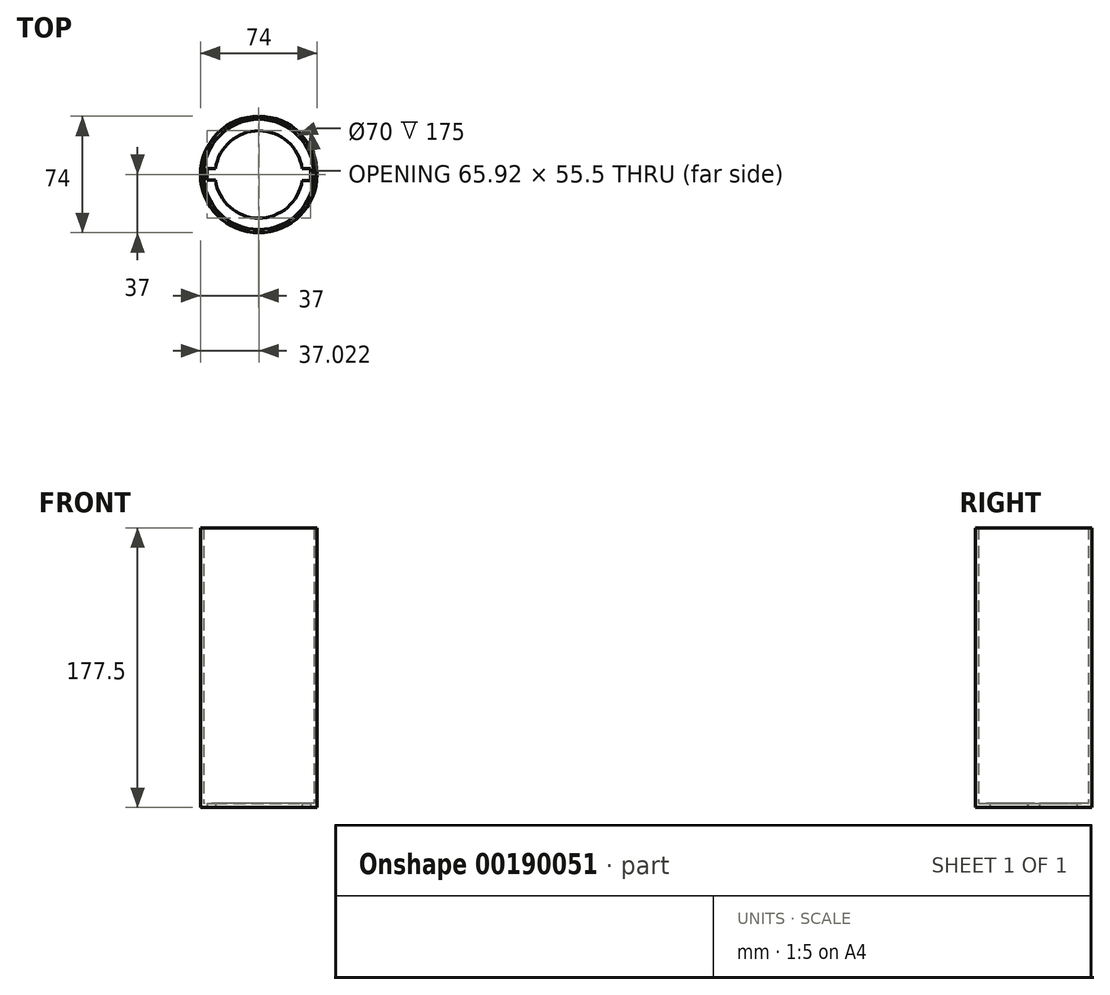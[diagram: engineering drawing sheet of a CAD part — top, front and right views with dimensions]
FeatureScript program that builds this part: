
annotation { "Feature Type Name" : "Feature", "Feature Type Description" : "" }
export const myFeature = defineFeature(function(context is Context, id is Id, definition is map)
    precondition{}
    {
        {
            var Q0;
            Q0=qCreatedBy(makeId("Top.planeOp"),FACE);
            var sketch = newSketch(context, id + "F0", { "sketchPlane" : qUnion([Q0])});
            skCircle(sketch, "E0", {"center": v(0, 0) * mm, "radius": 37 * mm});
            skLineSegment(sketch, "E1.bottom", {"start": v(27.48, -3.84) * mm, "end": v(32.98, -3.84) * mm});
            skLineSegment(sketch, "E1.top", {"start": v(27.48, 3.66) * mm, "end": v(32.98, 3.66) * mm});
            skLineSegment(sketch, "E1.right", {"start": v(32.98, -3.84) * mm, "end": v(32.98, 3.66) * mm});
            skLineSegment(sketch, "E2.bottom", {"start": v(-32.94, -3.62) * mm, "end": v(-27.44, -3.62) * mm});
            skLineSegment(sketch, "E2.top", {"start": v(-32.94, 3.88) * mm, "end": v(-27.44, 3.88) * mm});
            skLineSegment(sketch, "E2.left", {"start": v(-32.94, -3.62) * mm, "end": v(-32.94, 3.88) * mm});
            skPoint(sketch, "E3", {"position": v(-27.44, 3.88) * mm});
            skPoint(sketch, "E4", {"position": v(-27.44, -3.62) * mm});
            skArc(sketch, "E5", {"start": v(-27.51, -3.62) * mm, "mid": v(-0.11, -27.75) * mm, "end": v(27.48, -3.84) * mm});
            skArc(sketch, "E6", {"start": v(27.5, 3.66) * mm, "mid": v(0.11, 27.75) * mm, "end": v(-27.48, 3.88) * mm});
            skSolve(sketch);
        }
        {
            var Q0;
            Q0=makeQuery(id+"F0.imprint","IMPRINT",FACE,{"disambiguationData":[TD([[makeQuery(id+"F0.imprint","IMPRINT",EDGE,{"derivedFrom":sQuery(id+"F0.wireOp",EDGE,"E0")}),1.0]])]});
            extrude(context, id + "F1", {"entities" : qUnion([Q0]), "depth" : 2.5 * mm});
        }
        {
            var Q0;
            Q0=makeQuery(id+"F1.opExtrude","CAP_FACE",FACE,{"disambiguationData":[OSD([sQuery(id+"F0.wireOp",EDGE,"E0"),sQuery(id+"F0.wireOp",EDGE,"E1.bottom"),sQuery(id+"F0.wireOp",EDGE,"E1.top"),sQuery(id+"F0.wireOp",EDGE,"E1.right"),sQuery(id+"F0.wireOp",EDGE,"E2.bottom"),sQuery(id+"F0.wireOp",EDGE,"E2.top"),sQuery(id+"F0.wireOp",EDGE,"E2.left"),sQuery(id+"F0.wireOp",EDGE,"E5"),sQuery(id+"F0.wireOp",EDGE,"E6")])],"isStart":false});
            var sketch = newSketch(context, id + "F2", { "sketchPlane" : qUnion([Q0])});
            skCircle(sketch, "E7", {"center": v(0, 0) * mm, "radius": 35 * mm});
            skSolve(sketch);
        }
        {
            var Q0;
            Q0=makeQuery(id+"F2.imprint","IMPRINT",FACE,{"disambiguationData":[TD([[makeQuery(id+"F2.imprint","IMPRINT",EDGE,{"derivedFrom":sQuery(id+"F2.wireOp",EDGE,"E7")}),-1.0]])]});
            extrude(context, id + "F3", {"entities" : qUnion([Q0]), "operationType" : NewBodyOperationType.ADD, "depth" : 175 * mm});
        }
    });
